# Revit family: HeartFelt-Linear-Wire Suspension Set_HunterDouglasEurope.LOG200
name_source: partatom
category: Specialty Equipment
revit_build: Autodesk Revit 2016 (Build: 20150220_1215(x64)
units: mm (PartAtom-declared; Revit-internal decimal feet)

## family parameters
Always vertical = Yes
Cut with Voids When Loaded = No
OmniClass Number = 23.35.70.24.11.11.11
OmniClass Title = Suspended Ceilings, Suspension Assembly
Part Type = Normal
Room Calculation Point = No
Round Connector Dimension = Use Diameter
Shared = No
Work Plane-Based = No

## types (1)
- Wire Suspension Set
    EN13501-1_Fire rating = Class A1
    Instalation Instructions = https://www.gripple.co.uk
    Load Rating_Female Feet = 15kg @ 5:1 Safety Factor
    Load Rating_Top Hat = 45kg @ 5:1Safety Factor
    Manufacturer = Gripple
    Model = Wire Suspension Set
    Product Data = https://www.gripple.co.uk
    Product Line = HeartFelt® Linear
    Subcategory = HeartFelt® Ceilings
    URL = https://www.gripple.com

## geometry (parser evidence)
native form markers: Sweep x2
no freeform markers — native parametric forms only
